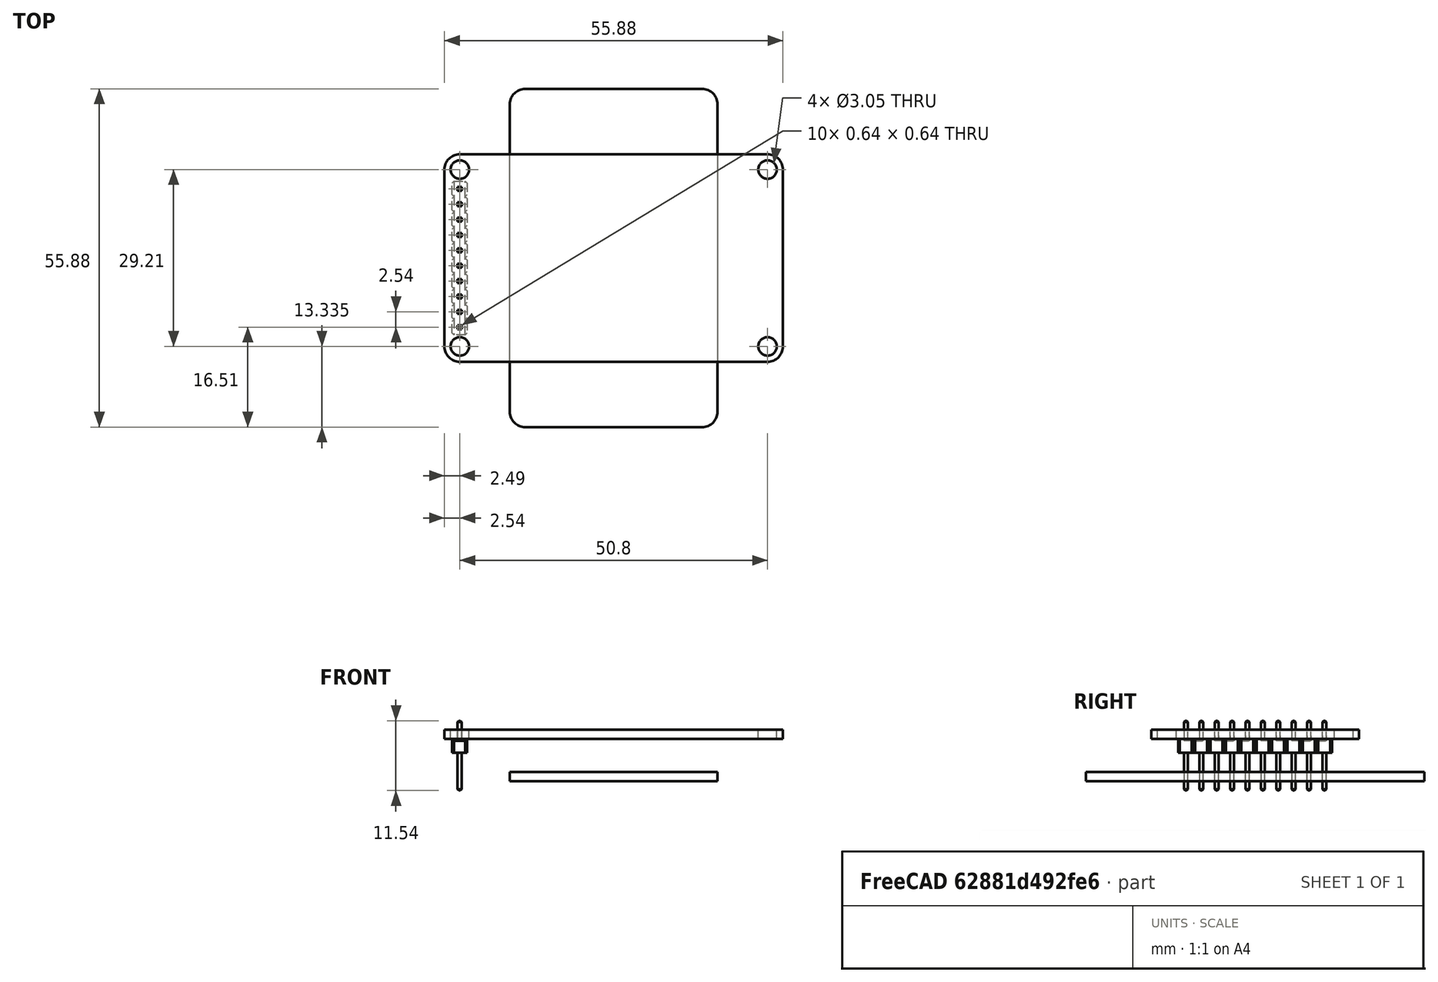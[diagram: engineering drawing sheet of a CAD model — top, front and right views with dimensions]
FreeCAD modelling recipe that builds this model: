
FCSTD DOCUMENT  (FreeCAD 0.16R5239 (Git))
Label: LCD_TFT
License: All rights reserved
LicenseURL: http://en.wikipedia.org/wiki/All_rights_reserved
objects: Part::Feature×2, Sketcher::SketchObject×2, PartDesign::Pad×1, PartDesign::Fillet×1
note: 7 computed .brp shape members not serialized (recipe doc carries the construction recipe); baked Part::Feature solids carry a one-line shape summary decoded from their .brp

FEATURE [Part::Feature] Shape005026  label="Fusion001"
  shape: bbox 2.49 x 25.4 x 11.54 mm, 302 faces (baked)
FEATURE [Part::Feature] Shape005033  label="Pocket"
  shape: bbox 55.88 x 34.29 x 1.524 mm, 14 faces (baked)
FEATURE [Sketcher::SketchObject] Sketch
  Support = -> Fillet [Face5]
  sketch-geometry (4):
    g0: LineSegment StartX=-17.145 StartY=27.94 StartZ=0 EndX=17.145 EndY=27.94 EndZ=0
    g1: LineSegment StartX=17.145 StartY=27.94 StartZ=0 EndX=17.145 EndY=-27.94 EndZ=0
    g2: LineSegment StartX=17.145 StartY=-27.94 StartZ=0 EndX=-17.145 EndY=-27.94 EndZ=0
    g3: LineSegment StartX=-17.145 StartY=-27.94 StartZ=0 EndX=-17.145 EndY=27.94 EndZ=0
  constraints (12):
    c: Coincident(g0,g1)
    c: Coincident(g1,g2)
    c: Coincident(g2,g3)
    c: Coincident(g3,g0)
    c: Horizontal(g0)
    c: Horizontal(g2)
    c: Vertical(g1)
    c: Vertical(g3)
    c: DistanceX(g0) = 34.29
    c: DistanceY(g3) = 55.88
    c: Symmetric(g0,g0,g-2)
    c: Symmetric(g0,g2,g-1)
FEATURE [PartDesign::Pad] Pad
  Length = 1.524
  Length2 = 100
  Sketch = -> Sketch
  Type = 0
FEATURE [PartDesign::Fillet] Fillet
  Base = -> Pad [Edge2,Edge5,Edge8,Edge1]
  Radius = 1
FEATURE [Sketcher::SketchObject] Sketch001
  Placement = pos=(0,0,1.524) rot=(0,0,1;0rad)
  Support = -> Fillet [Face5]
  sketch-geometry (4):
    g0: Circle CenterX=-14.605 CenterY=25.4 CenterZ=0 NormalX=0 NormalY=0 NormalZ=1 Radius=1.524
    g1: Circle CenterX=-14.605 CenterY=-25.4 CenterZ=0 NormalX=0 NormalY=0 NormalZ=1 Radius=1.524
    g2: Circle CenterX=14.605 CenterY=25.4 CenterZ=0 NormalX=0 NormalY=0 NormalZ=1 Radius=1.524
    g3: Circle CenterX=14.605 CenterY=-25.4 CenterZ=0 NormalX=0 NormalY=0 NormalZ=1 Radius=1.524
  constraints (9):
    c: Radius(g0) = 1.524
    c: Radius(g1) = 1.524
    c: Radius(g3) = 1.524
    c: Radius(g2) = 1.524
    c: Symmetric(g0,g2,g-2)
    c: Symmetric(g1,g3,g-2)
    c: Symmetric(g0,g1,g-1)
    c: DistanceX(g0,g2) = 29.21
    c: DistanceY(g0,g1) = -50.8
